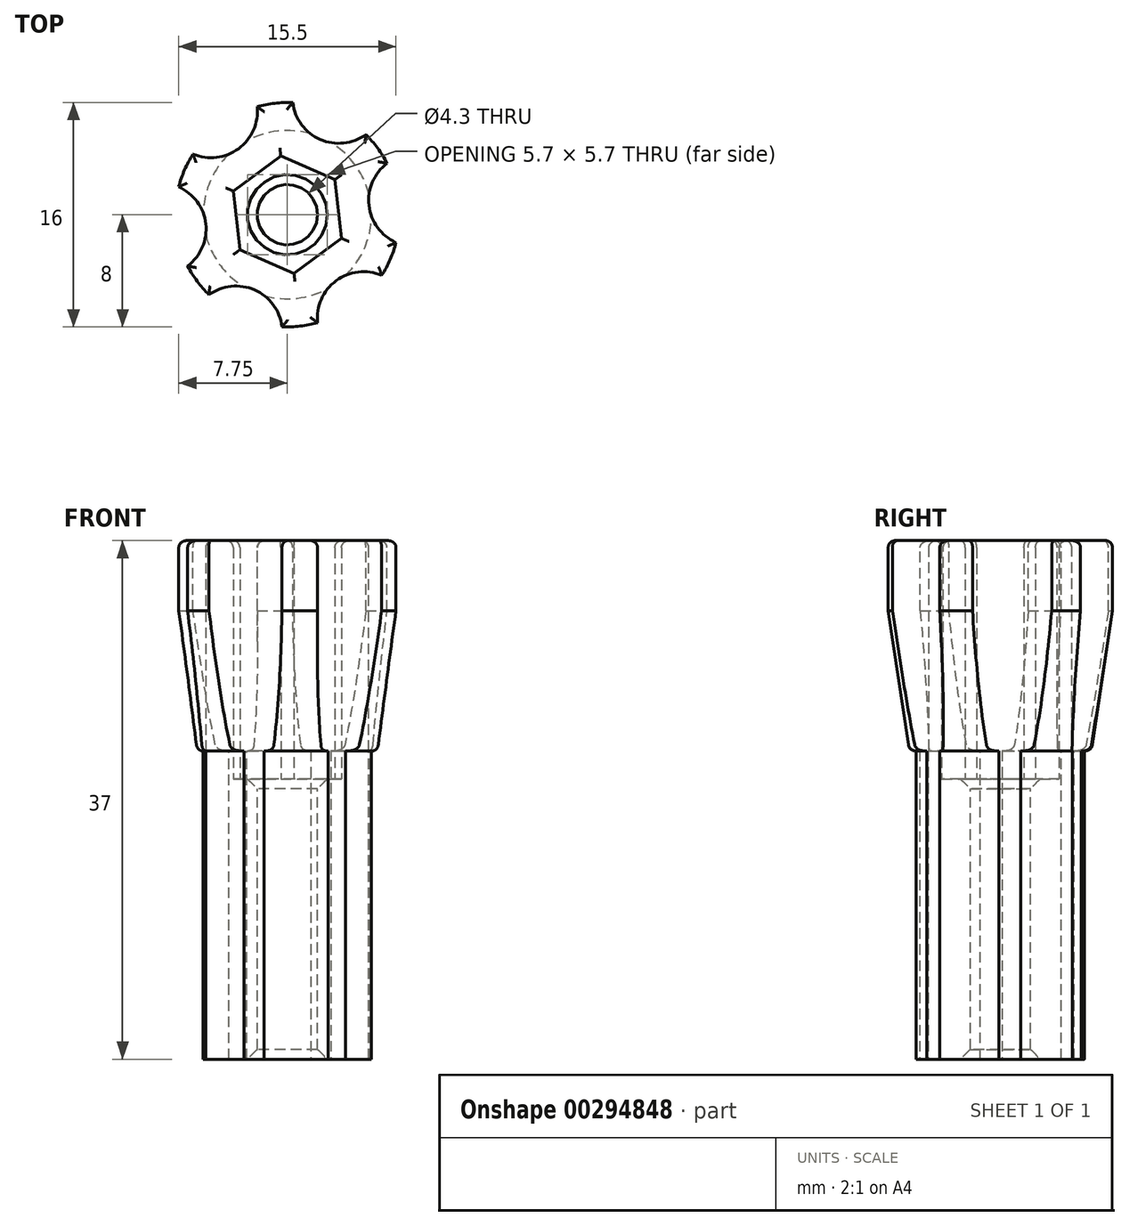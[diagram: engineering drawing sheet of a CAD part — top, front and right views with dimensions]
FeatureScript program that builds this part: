
annotation { "Feature Type Name" : "Feature", "Feature Type Description" : "" }
export const myFeature = defineFeature(function(context is Context, id is Id, definition is map)
    precondition{}
    {
        {
            var Q0;
            Q0=qCreatedBy(makeId("Top.planeOp"),FACE);
            var sketch = newSketch(context, id + "F0", { "sketchPlane" : qUnion([Q0])});
            skCircle(sketch, "E0", {"center": v(0, 0) * mm, "radius": 2.15 * mm});
            skCircle(sketch, "E1", {"center": v(0, 0) * mm, "radius": 6 * mm});
            skSolve(sketch);
        }
        {
            var Q0;
            Q0=makeQuery(id+"F0.imprint","IMPRINT",FACE,{"disambiguationData":[TD([[makeQuery(id+"F0.imprint","IMPRINT",EDGE,{"derivedFrom":sQuery(id+"F0.wireOp",EDGE,"E0")}),-1.0]])]});
            extrude(context, id + "F1", {"entities" : qUnion([Q0]), "depth" : 10 * mm});
        }
        {
            var Q0;
            Q0=qCreatedBy(makeId("Front.planeOp"),FACE);
            var sketch = newSketch(context, id + "F2", { "sketchPlane" : qUnion([Q0])});
            skLineSegment(sketch, "E2", {"start": v(0, 10) * mm, "end": v(0, 20) * mm});
            skLineSegment(sketch, "E3", {"start": v(0, 20) * mm, "end": v(8, 20) * mm});
            skLineSegment(sketch, "E4", {"start": v(8, 20) * mm, "end": v(0, 10) * mm});
            skLineSegment(sketch, "E5", {"start": v(0, 10) * mm, "end": v(6.5, 10) * mm});
            skLineSegment(sketch, "E6", {"start": v(6.5, 10) * mm, "end": v(8, 20) * mm});
            skLineSegment(sketch, "E7", {"start": v(0, 20) * mm, "end": v(2.1, 20) * mm});
            skLineSegment(sketch, "E8", {"start": v(2.1, 20) * mm, "end": v(2.1, 10) * mm});
            skSolve(sketch);
        }
        {
            var Q0;
            {var subQ0=sQuery(id+"F2.wireOp",EDGE,"E3");Q0=makeQuery(id+"F2.imprint","IMPRINT",FACE,{"disambiguationData":[TD([[makeQuery(id+"F2.imprint","IMPRINT",EDGE,{"derivedFrom":subQ0}),-1.0]])]});}
            var Q1;
            {var subQ0=sQuery(id+"F2.wireOp",EDGE,"E6");Q1=makeQuery(id+"F2.imprint","IMPRINT",FACE,{"disambiguationData":[TD([[makeQuery(id+"F2.imprint","IMPRINT",EDGE,{"derivedFrom":subQ0}),1.0]])]});}
            var Q2;
            Q2=sQuery(id+"F2.wireOp",EDGE,"E2");
            revolve(context, id + "F3", {"operationType" : NewBodyOperationType.ADD, "entities" : qUnion([Q0, Q1]), "axis" : qUnion([Q2]), "revolveType" : RevolveType.FULL});
        }
        {
            var Q0;
            Q0=makeQuery(id+"F3.opRevolve","SWEPT_FACE",FACE,{"disambiguationData":[OSD([sQuery(id+"F2.wireOp",EDGE,"E3")])]});
            var sketch = newSketch(context, id + "F4", { "sketchPlane" : qUnion([Q0])});
            skCircle(sketch, "E9.cCircle", {"center": v(0, 0) * mm, "radius": 5.25 * mm, "construction": true});
            skLineSegment(sketch, "E9.0", {"start": v(5.56, -2.42) * mm, "end": v(0.68, -6.02) * mm});
            skLineSegment(sketch, "E9.1", {"start": v(0.68, -6.02) * mm, "end": v(-4.88, -3.6) * mm});
            skLineSegment(sketch, "E9.2", {"start": v(-4.88, -3.6) * mm, "end": v(-5.56, 2.42) * mm});
            skLineSegment(sketch, "E9.3", {"start": v(-5.56, 2.42) * mm, "end": v(-0.68, 6.02) * mm});
            skLineSegment(sketch, "E9.4", {"start": v(-0.68, 6.02) * mm, "end": v(4.88, 3.6) * mm});
            skLineSegment(sketch, "E9.5", {"start": v(4.88, 3.6) * mm, "end": v(5.56, -2.42) * mm});
            skPoint(sketch, "E9.0.midPoint", {"position": v(3.12, -4.22) * mm});
            skCircle(sketch, "E10.cCircle", {"center": v(0, 0) * mm, "radius": 3.65 * mm, "construction": true});
            skLineSegment(sketch, "E10.0", {"start": v(-3.86, 1.69) * mm, "end": v(-0.47, 4.19) * mm});
            skLineSegment(sketch, "E10.1", {"start": v(-0.47, 4.19) * mm, "end": v(3.4, 2.5) * mm});
            skLineSegment(sketch, "E10.2", {"start": v(3.4, 2.5) * mm, "end": v(3.86, -1.69) * mm});
            skLineSegment(sketch, "E10.3", {"start": v(3.86, -1.69) * mm, "end": v(0.47, -4.19) * mm});
            skLineSegment(sketch, "E10.4", {"start": v(0.47, -4.19) * mm, "end": v(-3.4, -2.5) * mm});
            skLineSegment(sketch, "E10.5", {"start": v(-3.4, -2.5) * mm, "end": v(-3.86, 1.69) * mm});
            skPoint(sketch, "E10.0.midPoint", {"position": v(-2.17, 2.94) * mm});
            skSolve(sketch);
        }
        {
            var Q0;
            Q0=makeQuery(id+"F4.imprint","IMPRINT",FACE,{"disambiguationData":[TD([[makeQuery(id+"F4.imprint","IMPRINT",EDGE,{"derivedFrom":sQuery(id+"F4.wireOp",EDGE,"E9.0")}),1.0]])]});
            var Q1;
            Q1=makeQuery(id+"F4.imprint","IMPRINT",FACE,{"disambiguationData":[TD([[makeQuery(id+"F4.imprint","IMPRINT",EDGE,{"derivedFrom":sQuery(id+"F4.wireOp",EDGE,"E9.0")}),-1.0]])]});
            extrude(context, id + "F5", {"entities" : qUnion([Q0, Q1]), "operationType" : NewBodyOperationType.ADD, "depth" : 15 * mm});
        }
        {
            var Q0;
            Q0=makeQuery(id+"F5.opExtrude","CAP_FACE",FACE,{"disambiguationData":[OSD([sQuery(id+"F2.wireOp",EDGE,"E3"),sQuery(id+"F2.wireOp",EDGE,"E4"),sQuery(id+"F2.wireOp",EDGE,"E6"),sQuery(id+"F4.wireOp",EDGE,"E9.0"),sQuery(id+"F4.wireOp",EDGE,"E9.1"),sQuery(id+"F4.wireOp",EDGE,"E9.2"),sQuery(id+"F4.wireOp",EDGE,"E9.3"),sQuery(id+"F4.wireOp",EDGE,"E9.4"),sQuery(id+"F4.wireOp",EDGE,"E9.5")])],"isStart":false});
            var sketch = newSketch(context, id + "F6", { "sketchPlane" : qUnion([Q0])});
            skArc(sketch, "E11", {"start": v(1.46, 3.35) * mm, "mid": v(-0.92, 8.15) * mm, "end": v(-2.17, 2.94) * mm});
            skArc(sketch, "E12", {"start": v(-2.17, 2.94) * mm, "mid": v(-7.52, 3.28) * mm, "end": v(-3.63, -0.4) * mm});
            skArc(sketch, "E13", {"start": v(-6.73, 4.33) * mm, "mid": v(-3.48, 4.71) * mm, "end": v(-2.16, 7.7) * mm});
            skArc(sketch, "E14", {"start": v(-1.46, -3.35) * mm, "mid": v(0.92, -8.15) * mm, "end": v(2.17, -2.94) * mm});
            skArc(sketch, "E15", {"start": v(-3.63, -0.4) * mm, "mid": v(-6.6, -4.87) * mm, "end": v(-1.46, -3.35) * mm});
            skArc(sketch, "E16", {"start": v(2.17, -2.94) * mm, "mid": v(7.52, -3.28) * mm, "end": v(3.63, 0.4) * mm});
            skArc(sketch, "E17", {"start": v(3.63, 0.4) * mm, "mid": v(6.6, 4.87) * mm, "end": v(1.46, 3.35) * mm});
            skArc(sketch, "E18", {"start": v(0.39, 8) * mm, "mid": v(2.34, 5.37) * mm, "end": v(5.6, 5.72) * mm});
            skArc(sketch, "E19", {"start": v(7.11, 3.66) * mm, "mid": v(5.82, 0.66) * mm, "end": v(7.75, -1.99) * mm});
            skArc(sketch, "E20", {"start": v(6.73, -4.33) * mm, "mid": v(3.48, -4.71) * mm, "end": v(2.16, -7.7) * mm});
            skArc(sketch, "E21", {"start": v(-0.39, -8) * mm, "mid": v(-2.34, -5.37) * mm, "end": v(-5.6, -5.72) * mm});
            skArc(sketch, "E22", {"start": v(-7.11, -3.66) * mm, "mid": v(-5.82, -0.66) * mm, "end": v(-7.75, 1.99) * mm});
            skSolve(sketch);
        }
        {
            var Q0;
            {var subQ0=sQuery(id+"F6.wireOp",EDGE,"E13");var subQ1=sQuery(id+"F6.wireOp",EDGE,"E11");var subQ4=makeQuery(id+"F6.imprint","INTERSECT",VERTEX,{"derivedFrom":[subQ1,subQ0]});Q0=makeQuery(id+"F6.imprint","IMPRINT",FACE,{"disambiguationData":[TD([[makeQuery(id+"F6.imprint","IMPRINT",EDGE,{"disambiguationData":[TD([[subQ4,1.0]])],"derivedFrom":subQ0}),1.0]])]});}
            var Q1;
            {var subQ0=sQuery(id+"F6.wireOp",EDGE,"E13");var subQ1=sQuery(id+"F6.wireOp",EDGE,"E12");var subQ3=makeQuery(id+"F6.imprint","INTERSECT",VERTEX,{"derivedFrom":[subQ1,subQ0]});Q1=makeQuery(id+"F6.imprint","IMPRINT",FACE,{"disambiguationData":[TD([[makeQuery(id+"F6.imprint","IMPRINT",EDGE,{"disambiguationData":[TD([[subQ3,-1.0]])],"derivedFrom":subQ1}),1.0]])]});}
            var Q2;
            {var subQ0=sQuery(id+"F6.wireOp",EDGE,"E13");var subQ1=sQuery(id+"F6.wireOp",EDGE,"E11");var subQ3=makeQuery(id+"F6.imprint","INTERSECT",VERTEX,{"derivedFrom":[subQ1,subQ0]});Q2=makeQuery(id+"F6.imprint","IMPRINT",FACE,{"disambiguationData":[TD([[makeQuery(id+"F6.imprint","IMPRINT",EDGE,{"disambiguationData":[TD([[subQ3,1.0]])],"derivedFrom":subQ1}),1.0]])]});}
            var Q3;
            {var subQ0=sQuery(id+"F6.wireOp",EDGE,"E22");var subQ1=sQuery(id+"F6.wireOp",EDGE,"E12");var subQ4=makeQuery(id+"F6.imprint","INTERSECT",VERTEX,{"derivedFrom":[subQ1,subQ0]});Q3=makeQuery(id+"F6.imprint","IMPRINT",FACE,{"disambiguationData":[TD([[makeQuery(id+"F6.imprint","IMPRINT",EDGE,{"disambiguationData":[TD([[subQ4,1.0]])],"derivedFrom":subQ0}),1.0]])]});}
            var Q4;
            {var subQ0=sQuery(id+"F6.wireOp",EDGE,"E22");var subQ1=sQuery(id+"F6.wireOp",EDGE,"E12");var subQ3=makeQuery(id+"F6.imprint","INTERSECT",VERTEX,{"derivedFrom":[subQ1,subQ0]});Q4=makeQuery(id+"F6.imprint","IMPRINT",FACE,{"disambiguationData":[TD([[makeQuery(id+"F6.imprint","IMPRINT",EDGE,{"disambiguationData":[TD([[subQ3,1.0]])],"derivedFrom":subQ1}),1.0]])]});}
            var Q5;
            {var subQ0=sQuery(id+"F6.wireOp",EDGE,"E22");var subQ1=sQuery(id+"F6.wireOp",EDGE,"E15");var subQ3=makeQuery(id+"F6.imprint","INTERSECT",VERTEX,{"derivedFrom":[subQ1,subQ0]});Q5=makeQuery(id+"F6.imprint","IMPRINT",FACE,{"disambiguationData":[TD([[makeQuery(id+"F6.imprint","IMPRINT",EDGE,{"disambiguationData":[TD([[subQ3,-1.0]])],"derivedFrom":subQ1}),1.0]])]});}
            var Q6;
            {var subQ0=sQuery(id+"F6.wireOp",EDGE,"E21");var subQ1=sQuery(id+"F6.wireOp",EDGE,"E14");var subQ4=makeQuery(id+"F6.imprint","INTERSECT",VERTEX,{"derivedFrom":[subQ1,subQ0]});Q6=makeQuery(id+"F6.imprint","IMPRINT",FACE,{"disambiguationData":[TD([[makeQuery(id+"F6.imprint","IMPRINT",EDGE,{"disambiguationData":[TD([[subQ4,-1.0]])],"derivedFrom":subQ0}),1.0]])]});}
            var Q7;
            {var subQ0=sQuery(id+"F6.wireOp",EDGE,"E21");var subQ1=sQuery(id+"F6.wireOp",EDGE,"E15");var subQ3=makeQuery(id+"F6.imprint","INTERSECT",VERTEX,{"derivedFrom":[subQ1,subQ0]});Q7=makeQuery(id+"F6.imprint","IMPRINT",FACE,{"disambiguationData":[TD([[makeQuery(id+"F6.imprint","IMPRINT",EDGE,{"disambiguationData":[TD([[subQ3,1.0]])],"derivedFrom":subQ1}),1.0]])]});}
            var Q8;
            {var subQ0=sQuery(id+"F6.wireOp",EDGE,"E21");var subQ1=sQuery(id+"F6.wireOp",EDGE,"E14");var subQ3=makeQuery(id+"F6.imprint","INTERSECT",VERTEX,{"derivedFrom":[subQ1,subQ0]});Q8=makeQuery(id+"F6.imprint","IMPRINT",FACE,{"disambiguationData":[TD([[makeQuery(id+"F6.imprint","IMPRINT",EDGE,{"disambiguationData":[TD([[subQ3,-1.0]])],"derivedFrom":subQ1}),1.0]])]});}
            var Q9;
            {var subQ0=sQuery(id+"F6.wireOp",EDGE,"E20");var subQ1=sQuery(id+"F6.wireOp",EDGE,"E14");var subQ4=makeQuery(id+"F6.imprint","INTERSECT",VERTEX,{"derivedFrom":[subQ1,subQ0]});Q9=makeQuery(id+"F6.imprint","IMPRINT",FACE,{"disambiguationData":[TD([[makeQuery(id+"F6.imprint","IMPRINT",EDGE,{"disambiguationData":[TD([[subQ4,1.0]])],"derivedFrom":subQ0}),1.0]])]});}
            var Q10;
            {var subQ0=sQuery(id+"F6.wireOp",EDGE,"E20");var subQ1=sQuery(id+"F6.wireOp",EDGE,"E16");var subQ3=makeQuery(id+"F6.imprint","INTERSECT",VERTEX,{"derivedFrom":[subQ1,subQ0]});Q10=makeQuery(id+"F6.imprint","IMPRINT",FACE,{"disambiguationData":[TD([[makeQuery(id+"F6.imprint","IMPRINT",EDGE,{"disambiguationData":[TD([[subQ3,-1.0]])],"derivedFrom":subQ1}),1.0]])]});}
            var Q11;
            {var subQ0=sQuery(id+"F6.wireOp",EDGE,"E20");var subQ1=sQuery(id+"F6.wireOp",EDGE,"E14");var subQ3=makeQuery(id+"F6.imprint","INTERSECT",VERTEX,{"derivedFrom":[subQ1,subQ0]});Q11=makeQuery(id+"F6.imprint","IMPRINT",FACE,{"disambiguationData":[TD([[makeQuery(id+"F6.imprint","IMPRINT",EDGE,{"disambiguationData":[TD([[subQ3,1.0]])],"derivedFrom":subQ1}),1.0]])]});}
            var Q12;
            {var subQ0=sQuery(id+"F6.wireOp",EDGE,"E19");var subQ1=sQuery(id+"F6.wireOp",EDGE,"E16");var subQ4=makeQuery(id+"F6.imprint","INTERSECT",VERTEX,{"derivedFrom":[subQ1,subQ0]});Q12=makeQuery(id+"F6.imprint","IMPRINT",FACE,{"disambiguationData":[TD([[makeQuery(id+"F6.imprint","IMPRINT",EDGE,{"disambiguationData":[TD([[subQ4,1.0]])],"derivedFrom":subQ0}),1.0]])]});}
            var Q13;
            {var subQ0=sQuery(id+"F6.wireOp",EDGE,"E19");var subQ1=sQuery(id+"F6.wireOp",EDGE,"E16");var subQ3=makeQuery(id+"F6.imprint","INTERSECT",VERTEX,{"derivedFrom":[subQ1,subQ0]});Q13=makeQuery(id+"F6.imprint","IMPRINT",FACE,{"disambiguationData":[TD([[makeQuery(id+"F6.imprint","IMPRINT",EDGE,{"disambiguationData":[TD([[subQ3,1.0]])],"derivedFrom":subQ1}),1.0]])]});}
            var Q14;
            {var subQ0=sQuery(id+"F6.wireOp",EDGE,"E19");var subQ1=sQuery(id+"F6.wireOp",EDGE,"E17");var subQ3=makeQuery(id+"F6.imprint","INTERSECT",VERTEX,{"derivedFrom":[subQ1,subQ0]});Q14=makeQuery(id+"F6.imprint","IMPRINT",FACE,{"disambiguationData":[TD([[makeQuery(id+"F6.imprint","IMPRINT",EDGE,{"disambiguationData":[TD([[subQ3,-1.0]])],"derivedFrom":subQ1}),1.0]])]});}
            var Q15;
            {var subQ0=sQuery(id+"F6.wireOp",EDGE,"E18");var subQ1=sQuery(id+"F6.wireOp",EDGE,"E11");var subQ4=makeQuery(id+"F6.imprint","INTERSECT",VERTEX,{"derivedFrom":[subQ1,subQ0]});Q15=makeQuery(id+"F6.imprint","IMPRINT",FACE,{"disambiguationData":[TD([[makeQuery(id+"F6.imprint","IMPRINT",EDGE,{"disambiguationData":[TD([[subQ4,-1.0]])],"derivedFrom":subQ0}),1.0]])]});}
            var Q16;
            {var subQ0=sQuery(id+"F6.wireOp",EDGE,"E18");var subQ1=sQuery(id+"F6.wireOp",EDGE,"E11");var subQ3=makeQuery(id+"F6.imprint","INTERSECT",VERTEX,{"derivedFrom":[subQ1,subQ0]});Q16=makeQuery(id+"F6.imprint","IMPRINT",FACE,{"disambiguationData":[TD([[makeQuery(id+"F6.imprint","IMPRINT",EDGE,{"disambiguationData":[TD([[subQ3,-1.0]])],"derivedFrom":subQ1}),1.0]])]});}
            var Q17;
            {var subQ0=sQuery(id+"F6.wireOp",EDGE,"E18");var subQ1=sQuery(id+"F6.wireOp",EDGE,"E17");var subQ3=makeQuery(id+"F6.imprint","INTERSECT",VERTEX,{"derivedFrom":[subQ1,subQ0]});Q17=makeQuery(id+"F6.imprint","IMPRINT",FACE,{"disambiguationData":[TD([[makeQuery(id+"F6.imprint","IMPRINT",EDGE,{"disambiguationData":[TD([[subQ3,1.0]])],"derivedFrom":subQ1}),1.0]])]});}
            extrude(context, id + "F7", {"entities" : qUnion([Q0, Q1, Q2, Q3, Q4, Q5, Q6, Q7, Q8, Q9, Q10, Q11, Q12, Q13, Q14, Q15, Q16, Q17]), "operationType" : NewBodyOperationType.REMOVE, "oppositeDirection" : true, "depth" : 25 * mm});
        }
        {
            var Q0;
            Q0=makeQuery(id+"F5.opExtrude","CAP_FACE",FACE,{"disambiguationData":[OSD([sQuery(id+"F2.wireOp",EDGE,"E3"),sQuery(id+"F2.wireOp",EDGE,"E4"),sQuery(id+"F2.wireOp",EDGE,"E6"),sQuery(id+"F4.wireOp",EDGE,"E9.0"),sQuery(id+"F4.wireOp",EDGE,"E9.1"),sQuery(id+"F4.wireOp",EDGE,"E9.2"),sQuery(id+"F4.wireOp",EDGE,"E9.3"),sQuery(id+"F4.wireOp",EDGE,"E9.4"),sQuery(id+"F4.wireOp",EDGE,"E9.5")])],"isStart":false});
            extrude(context, id + "F8", {"entities" : qUnion([Q0]), "operationType" : NewBodyOperationType.REMOVE, "oppositeDirection" : true, "depth" : 5 * mm});
        }
        {
            var Q0;
            Q0=makeQuery(id+"F1.opExtrude","CAP_FACE",FACE,{"disambiguationData":[OSD([sQuery(id+"F0.wireOp",EDGE,"E0"),sQuery(id+"F0.wireOp",EDGE,"E1")])],"isStart":true});
            extrude(context, id + "F9", {"entities" : qUnion([Q0]), "operationType" : NewBodyOperationType.REMOVE, "oppositeDirection" : true, "depth" : 10 * mm});
        }
        {
            var Q0;
            Q0=makeQuery(id+"F8.boolean.opBoolean","COPY",FACE,{"derivedFrom":makeQuery(id+"F8.opExtrude","CAP_FACE",FACE,{"disambiguationData":[OSD([sQuery(id+"F2.wireOp",EDGE,"E3"),sQuery(id+"F2.wireOp",EDGE,"E4"),sQuery(id+"F2.wireOp",EDGE,"E6"),sQuery(id+"F4.wireOp",EDGE,"E10.0"),sQuery(id+"F4.wireOp",EDGE,"E10.1"),sQuery(id+"F4.wireOp",EDGE,"E10.2"),sQuery(id+"F4.wireOp",EDGE,"E10.3"),sQuery(id+"F4.wireOp",EDGE,"E10.4"),sQuery(id+"F4.wireOp",EDGE,"E10.5")])],"isStart":false})});
            extrude(context, id + "F10", {"entities" : qUnion([Q0]), "operationType" : NewBodyOperationType.REMOVE, "oppositeDirection" : true, "depth" : 5 * mm});
        }
        {
            var Q0;
            {var subQ0=sQuery(id+"F2.wireOp",EDGE,"E6");var subQ1=sQuery(id+"F2.wireOp",EDGE,"E4");var subQ2=sQuery(id+"F2.wireOp",EDGE,"E3");var subQ3=sQuery(id+"F6.wireOp",EDGE,"E21");var subQ5=makeQuery(id+"F5.opExtrude","CAP_EDGE",EDGE,{"disambiguationData":[OSD([subQ2,subQ1,subQ0])],"isStart":false});Q0=makeQuery(id+"F10.boolean.opBoolean","COPY",EDGE,{"derivedFrom":makeQuery(id+"F10.opExtrude","CAP_EDGE",EDGE,{"disambiguationData":[OSD([subQ2,subQ1,subQ0]),TDD([makeQuery(id+"F8.boolean.opBoolean","COPY",EDGE,{"derivedFrom":makeQuery(id+"F8.opExtrude","CAP_EDGE",EDGE,{"disambiguationData":[OSD([subQ2,subQ1,subQ0]),TDD([makeQuery(id+"F7.boolean.opBoolean","SPLIT",EDGE,{"disambiguationData":[TD([makeQuery(id+"F7.opExtrude","SWEPT_FACE",FACE,{"disambiguationData":[OSD([subQ3]),TDD([makeQuery(id+"F6.imprint","IMPRINT",EDGE,{"disambiguationData":[TD([[makeQuery(id+"F6.imprint","INTERSECT",VERTEX,{"derivedFrom":[sQuery(id+"F6.wireOp",EDGE,"E14"),subQ3]}),-1.0]])],"derivedFrom":subQ3})])]})])],"derivedFrom":subQ5})])],"isStart":false})})])],"isStart":false})});}
            var Q1;
            {var subQ0=sQuery(id+"F2.wireOp",EDGE,"E6");var subQ1=sQuery(id+"F2.wireOp",EDGE,"E4");var subQ2=sQuery(id+"F2.wireOp",EDGE,"E3");var subQ3=sQuery(id+"F6.wireOp",EDGE,"E20");var subQ5=makeQuery(id+"F5.opExtrude","CAP_EDGE",EDGE,{"disambiguationData":[OSD([subQ2,subQ1,subQ0])],"isStart":false});Q1=makeQuery(id+"F10.boolean.opBoolean","COPY",EDGE,{"derivedFrom":makeQuery(id+"F10.opExtrude","CAP_EDGE",EDGE,{"disambiguationData":[OSD([subQ2,subQ1,subQ0]),TDD([makeQuery(id+"F8.boolean.opBoolean","COPY",EDGE,{"derivedFrom":makeQuery(id+"F8.opExtrude","CAP_EDGE",EDGE,{"disambiguationData":[OSD([subQ2,subQ1,subQ0]),TDD([makeQuery(id+"F7.boolean.opBoolean","SPLIT",EDGE,{"disambiguationData":[TD([makeQuery(id+"F7.opExtrude","SWEPT_FACE",FACE,{"disambiguationData":[OSD([subQ3]),TDD([makeQuery(id+"F6.imprint","IMPRINT",EDGE,{"disambiguationData":[TD([[makeQuery(id+"F6.imprint","INTERSECT",VERTEX,{"derivedFrom":[sQuery(id+"F6.wireOp",EDGE,"E16"),subQ3]}),-1.0]])],"derivedFrom":subQ3})])]})])],"derivedFrom":subQ5})])],"isStart":false})})])],"isStart":false})});}
            var Q2;
            {var subQ0=sQuery(id+"F2.wireOp",EDGE,"E6");var subQ1=sQuery(id+"F2.wireOp",EDGE,"E4");var subQ2=sQuery(id+"F2.wireOp",EDGE,"E3");var subQ3=sQuery(id+"F6.wireOp",EDGE,"E19");var subQ5=makeQuery(id+"F5.opExtrude","CAP_EDGE",EDGE,{"disambiguationData":[OSD([subQ2,subQ1,subQ0])],"isStart":false});Q2=makeQuery(id+"F10.boolean.opBoolean","COPY",EDGE,{"derivedFrom":makeQuery(id+"F10.opExtrude","CAP_EDGE",EDGE,{"disambiguationData":[OSD([subQ2,subQ1,subQ0]),TDD([makeQuery(id+"F8.boolean.opBoolean","COPY",EDGE,{"derivedFrom":makeQuery(id+"F8.opExtrude","CAP_EDGE",EDGE,{"disambiguationData":[OSD([subQ2,subQ1,subQ0]),TDD([makeQuery(id+"F7.boolean.opBoolean","SPLIT",EDGE,{"disambiguationData":[TD([makeQuery(id+"F7.opExtrude","SWEPT_FACE",FACE,{"disambiguationData":[OSD([subQ3]),TDD([makeQuery(id+"F6.imprint","IMPRINT",EDGE,{"disambiguationData":[TD([[makeQuery(id+"F6.imprint","INTERSECT",VERTEX,{"derivedFrom":[sQuery(id+"F6.wireOp",EDGE,"E17"),subQ3]}),-1.0]])],"derivedFrom":subQ3})])]})])],"derivedFrom":subQ5})])],"isStart":false})})])],"isStart":false})});}
            var Q3;
            {var subQ0=sQuery(id+"F2.wireOp",EDGE,"E6");var subQ1=sQuery(id+"F2.wireOp",EDGE,"E4");var subQ2=sQuery(id+"F2.wireOp",EDGE,"E3");var subQ5=makeQuery(id+"F5.opExtrude","CAP_EDGE",EDGE,{"disambiguationData":[OSD([subQ2,subQ1,subQ0])],"isStart":false});var subQ6=sQuery(id+"F6.wireOp",EDGE,"E18");Q3=makeQuery(id+"F10.boolean.opBoolean","COPY",EDGE,{"derivedFrom":makeQuery(id+"F10.opExtrude","CAP_EDGE",EDGE,{"disambiguationData":[OSD([subQ2,subQ1,subQ0]),TDD([makeQuery(id+"F8.boolean.opBoolean","COPY",EDGE,{"derivedFrom":makeQuery(id+"F8.opExtrude","CAP_EDGE",EDGE,{"disambiguationData":[OSD([subQ2,subQ1,subQ0]),TDD([makeQuery(id+"F7.boolean.opBoolean","SPLIT",EDGE,{"disambiguationData":[TD([makeQuery(id+"F7.opExtrude","SWEPT_FACE",FACE,{"disambiguationData":[OSD([subQ6]),TDD([makeQuery(id+"F6.imprint","IMPRINT",EDGE,{"disambiguationData":[TD([[makeQuery(id+"F6.imprint","INTERSECT",VERTEX,{"derivedFrom":[sQuery(id+"F6.wireOp",EDGE,"E11"),subQ6]}),-1.0]])],"derivedFrom":subQ6})])]})])],"derivedFrom":subQ5})])],"isStart":false})})])],"isStart":false})});}
            var Q4;
            {var subQ0=sQuery(id+"F2.wireOp",EDGE,"E6");var subQ1=sQuery(id+"F2.wireOp",EDGE,"E4");var subQ2=sQuery(id+"F2.wireOp",EDGE,"E3");var subQ3=sQuery(id+"F6.wireOp",EDGE,"E13");var subQ5=makeQuery(id+"F5.opExtrude","CAP_EDGE",EDGE,{"disambiguationData":[OSD([subQ2,subQ1,subQ0])],"isStart":false});Q4=makeQuery(id+"F10.boolean.opBoolean","COPY",EDGE,{"derivedFrom":makeQuery(id+"F10.opExtrude","CAP_EDGE",EDGE,{"disambiguationData":[OSD([subQ2,subQ1,subQ0]),TDD([makeQuery(id+"F8.boolean.opBoolean","COPY",EDGE,{"derivedFrom":makeQuery(id+"F8.opExtrude","CAP_EDGE",EDGE,{"disambiguationData":[OSD([subQ2,subQ1,subQ0]),TDD([makeQuery(id+"F7.boolean.opBoolean","SPLIT",EDGE,{"disambiguationData":[TD([makeQuery(id+"F7.opExtrude","SWEPT_FACE",FACE,{"disambiguationData":[OSD([subQ3]),TDD([makeQuery(id+"F6.imprint","IMPRINT",EDGE,{"disambiguationData":[TD([[makeQuery(id+"F6.imprint","INTERSECT",VERTEX,{"derivedFrom":[sQuery(id+"F6.wireOp",EDGE,"E12"),subQ3]}),-1.0]])],"derivedFrom":subQ3})])]})])],"derivedFrom":subQ5})])],"isStart":false})})])],"isStart":false})});}
            var Q5;
            {var subQ0=sQuery(id+"F2.wireOp",EDGE,"E6");var subQ1=sQuery(id+"F2.wireOp",EDGE,"E4");var subQ2=sQuery(id+"F2.wireOp",EDGE,"E3");var subQ3=sQuery(id+"F6.wireOp",EDGE,"E13");var subQ5=makeQuery(id+"F5.opExtrude","CAP_EDGE",EDGE,{"disambiguationData":[OSD([subQ2,subQ1,subQ0])],"isStart":false});Q5=makeQuery(id+"F10.boolean.opBoolean","COPY",EDGE,{"derivedFrom":makeQuery(id+"F10.opExtrude","CAP_EDGE",EDGE,{"disambiguationData":[OSD([subQ2,subQ1,subQ0]),TDD([makeQuery(id+"F8.boolean.opBoolean","COPY",EDGE,{"derivedFrom":makeQuery(id+"F8.opExtrude","CAP_EDGE",EDGE,{"disambiguationData":[OSD([subQ2,subQ1,subQ0]),TDD([makeQuery(id+"F7.boolean.opBoolean","SPLIT",EDGE,{"disambiguationData":[TD([makeQuery(id+"F7.opExtrude","SWEPT_FACE",FACE,{"disambiguationData":[OSD([subQ3]),TDD([makeQuery(id+"F6.imprint","IMPRINT",EDGE,{"disambiguationData":[TD([[makeQuery(id+"F6.imprint","INTERSECT",VERTEX,{"derivedFrom":[sQuery(id+"F6.wireOp",EDGE,"E11"),subQ3]}),1.0]])],"derivedFrom":subQ3})])]})])],"derivedFrom":subQ5})])],"isStart":false})})])],"isStart":false})});}
            var Q6;
            Q6=makeQuery(id+"F10.boolean.opBoolean","COPY",EDGE,{"derivedFrom":makeQuery(id+"F10.opExtrude","CAP_EDGE",EDGE,{"disambiguationData":[OSD([sQuery(id+"F6.wireOp",EDGE,"E21")])],"isStart":false})});
            var Q7;
            Q7=makeQuery(id+"F10.boolean.opBoolean","COPY",FACE,{"derivedFrom":makeQuery(id+"F10.opExtrude","CAP_FACE",FACE,{"disambiguationData":[OSD([sQuery(id+"F2.wireOp",EDGE,"E3"),sQuery(id+"F2.wireOp",EDGE,"E4"),sQuery(id+"F2.wireOp",EDGE,"E6"),sQuery(id+"F4.wireOp",EDGE,"E10.0"),sQuery(id+"F4.wireOp",EDGE,"E10.1"),sQuery(id+"F4.wireOp",EDGE,"E10.2"),sQuery(id+"F4.wireOp",EDGE,"E10.3"),sQuery(id+"F4.wireOp",EDGE,"E10.4"),sQuery(id+"F4.wireOp",EDGE,"E10.5")])],"isStart":false})});
            fillet(context, id + "F11", {"entities" : qUnion([Q0, Q1, Q2, Q3, Q4, Q5, Q6, Q7]), "radius" : 0.5 * mm, "tangentPropagation" : true, "allowEdgeOverflow" : false});
        }
        {
            var Q0;
            {var subQ0=sQuery(id+"F2.wireOp",EDGE,"E5");var subQ1=sQuery(id+"F2.wireOp",EDGE,"E6");Q0=makeQuery(id+"F7.boolean.opBoolean","SPLIT",EDGE,{"disambiguationData":[TD([makeQuery(id+"F3.opRevolve","SWEPT_FACE",FACE,{"disambiguationData":[OSD([subQ0])]}),makeQuery(id+"F3.opRevolve","SWEPT_FACE",FACE,{"disambiguationData":[OSD([subQ1])]}),makeQuery(id+"F7.opExtrude","SWEPT_FACE",FACE,{"disambiguationData":[OSD([sQuery(id+"F6.wireOp",EDGE,"E13")])]}),makeQuery(id+"F7.opExtrude","SWEPT_FACE",FACE,{"disambiguationData":[OSD([sQuery(id+"F6.wireOp",EDGE,"E18")])]})])],"derivedFrom":makeQuery(id+"F3.opRevolve","SWEPT_EDGE",EDGE,{"disambiguationData":[OSD([subQ0,subQ1])]})});}
            var Q1;
            {var subQ0=sQuery(id+"F2.wireOp",EDGE,"E5");var subQ1=sQuery(id+"F2.wireOp",EDGE,"E6");Q1=makeQuery(id+"F7.boolean.opBoolean","SPLIT",EDGE,{"disambiguationData":[TD([makeQuery(id+"F3.opRevolve","SWEPT_FACE",FACE,{"disambiguationData":[OSD([subQ0])]}),makeQuery(id+"F3.opRevolve","SWEPT_FACE",FACE,{"disambiguationData":[OSD([subQ1])]}),makeQuery(id+"F7.opExtrude","SWEPT_FACE",FACE,{"disambiguationData":[OSD([sQuery(id+"F6.wireOp",EDGE,"E18")])]}),makeQuery(id+"F7.opExtrude","SWEPT_FACE",FACE,{"disambiguationData":[OSD([sQuery(id+"F6.wireOp",EDGE,"E19")])]})])],"derivedFrom":makeQuery(id+"F3.opRevolve","SWEPT_EDGE",EDGE,{"disambiguationData":[OSD([subQ0,subQ1])]})});}
            var Q2;
            {var subQ0=sQuery(id+"F2.wireOp",EDGE,"E5");var subQ1=sQuery(id+"F2.wireOp",EDGE,"E6");Q2=makeQuery(id+"F7.boolean.opBoolean","SPLIT",EDGE,{"disambiguationData":[TD([makeQuery(id+"F3.opRevolve","SWEPT_FACE",FACE,{"disambiguationData":[OSD([subQ0])]}),makeQuery(id+"F3.opRevolve","SWEPT_FACE",FACE,{"disambiguationData":[OSD([subQ1])]}),makeQuery(id+"F7.opExtrude","SWEPT_FACE",FACE,{"disambiguationData":[OSD([sQuery(id+"F6.wireOp",EDGE,"E13")])]}),makeQuery(id+"F7.opExtrude","SWEPT_FACE",FACE,{"disambiguationData":[OSD([sQuery(id+"F6.wireOp",EDGE,"E22")])]})])],"derivedFrom":makeQuery(id+"F3.opRevolve","SWEPT_EDGE",EDGE,{"disambiguationData":[OSD([subQ0,subQ1])]})});}
            var Q3;
            {var subQ0=sQuery(id+"F2.wireOp",EDGE,"E5");var subQ1=sQuery(id+"F2.wireOp",EDGE,"E6");Q3=makeQuery(id+"F7.boolean.opBoolean","SPLIT",EDGE,{"disambiguationData":[TD([makeQuery(id+"F3.opRevolve","SWEPT_FACE",FACE,{"disambiguationData":[OSD([subQ0])]}),makeQuery(id+"F3.opRevolve","SWEPT_FACE",FACE,{"disambiguationData":[OSD([subQ1])]}),makeQuery(id+"F7.opExtrude","SWEPT_FACE",FACE,{"disambiguationData":[OSD([sQuery(id+"F6.wireOp",EDGE,"E21")])]}),makeQuery(id+"F7.opExtrude","SWEPT_FACE",FACE,{"disambiguationData":[OSD([sQuery(id+"F6.wireOp",EDGE,"E22")])]})])],"derivedFrom":makeQuery(id+"F3.opRevolve","SWEPT_EDGE",EDGE,{"disambiguationData":[OSD([subQ0,subQ1])]})});}
            var Q4;
            {var subQ0=sQuery(id+"F2.wireOp",EDGE,"E5");var subQ1=sQuery(id+"F2.wireOp",EDGE,"E6");Q4=makeQuery(id+"F7.boolean.opBoolean","SPLIT",EDGE,{"disambiguationData":[TD([makeQuery(id+"F3.opRevolve","SWEPT_FACE",FACE,{"disambiguationData":[OSD([subQ0])]}),makeQuery(id+"F3.opRevolve","SWEPT_FACE",FACE,{"disambiguationData":[OSD([subQ1])]}),makeQuery(id+"F7.opExtrude","SWEPT_FACE",FACE,{"disambiguationData":[OSD([sQuery(id+"F6.wireOp",EDGE,"E20")])]}),makeQuery(id+"F7.opExtrude","SWEPT_FACE",FACE,{"disambiguationData":[OSD([sQuery(id+"F6.wireOp",EDGE,"E21")])]})])],"derivedFrom":makeQuery(id+"F3.opRevolve","SWEPT_EDGE",EDGE,{"disambiguationData":[OSD([subQ0,subQ1])]})});}
            var Q5;
            {var subQ0=sQuery(id+"F2.wireOp",EDGE,"E5");var subQ1=sQuery(id+"F2.wireOp",EDGE,"E6");Q5=makeQuery(id+"F7.boolean.opBoolean","SPLIT",EDGE,{"disambiguationData":[TD([makeQuery(id+"F3.opRevolve","SWEPT_FACE",FACE,{"disambiguationData":[OSD([subQ0])]}),makeQuery(id+"F3.opRevolve","SWEPT_FACE",FACE,{"disambiguationData":[OSD([subQ1])]}),makeQuery(id+"F7.opExtrude","SWEPT_FACE",FACE,{"disambiguationData":[OSD([sQuery(id+"F6.wireOp",EDGE,"E19")])]}),makeQuery(id+"F7.opExtrude","SWEPT_FACE",FACE,{"disambiguationData":[OSD([sQuery(id+"F6.wireOp",EDGE,"E20")])]})])],"derivedFrom":makeQuery(id+"F3.opRevolve","SWEPT_EDGE",EDGE,{"disambiguationData":[OSD([subQ0,subQ1])]})});}
            var Q6;
            {var subQ0=sQuery(id+"F6.wireOp",EDGE,"E22");Q6=makeQuery(id+"F7.boolean.opBoolean","COPY",EDGE,{"disambiguationData":[topologyDisambiguationEdgeConnected([makeQuery(id+"F7.opExtrude","SWEPT_FACE",FACE,{"disambiguationData":[OSD([subQ0])]}),makeQuery(id+"F7.opExtrude","CAP_FACE",FACE,{"disambiguationData":[OSD([sQuery(id+"F2.wireOp",EDGE,"E3"),sQuery(id+"F2.wireOp",EDGE,"E4"),sQuery(id+"F2.wireOp",EDGE,"E6"),subQ0])],"isStart":false})])],"derivedFrom":makeQuery(id+"F7.opExtrude","CAP_EDGE",EDGE,{"disambiguationData":[OSD([subQ0])],"isStart":false})});}
            var Q7;
            {var subQ0=sQuery(id+"F6.wireOp",EDGE,"E21");Q7=makeQuery(id+"F7.boolean.opBoolean","COPY",EDGE,{"disambiguationData":[topologyDisambiguationEdgeConnected([makeQuery(id+"F7.opExtrude","SWEPT_FACE",FACE,{"disambiguationData":[OSD([subQ0])]}),makeQuery(id+"F7.opExtrude","CAP_FACE",FACE,{"disambiguationData":[OSD([sQuery(id+"F2.wireOp",EDGE,"E3"),sQuery(id+"F2.wireOp",EDGE,"E4"),sQuery(id+"F2.wireOp",EDGE,"E6"),subQ0])],"isStart":false})])],"derivedFrom":makeQuery(id+"F7.opExtrude","CAP_EDGE",EDGE,{"disambiguationData":[OSD([subQ0])],"isStart":false})});}
            var Q8;
            {var subQ0=sQuery(id+"F6.wireOp",EDGE,"E20");Q8=makeQuery(id+"F7.boolean.opBoolean","COPY",EDGE,{"disambiguationData":[topologyDisambiguationEdgeConnected([makeQuery(id+"F7.opExtrude","SWEPT_FACE",FACE,{"disambiguationData":[OSD([subQ0])]}),makeQuery(id+"F7.opExtrude","CAP_FACE",FACE,{"disambiguationData":[OSD([sQuery(id+"F2.wireOp",EDGE,"E3"),sQuery(id+"F2.wireOp",EDGE,"E4"),sQuery(id+"F2.wireOp",EDGE,"E6"),subQ0])],"isStart":false})])],"derivedFrom":makeQuery(id+"F7.opExtrude","CAP_EDGE",EDGE,{"disambiguationData":[OSD([subQ0])],"isStart":false})});}
            var Q9;
            {var subQ0=sQuery(id+"F6.wireOp",EDGE,"E19");Q9=makeQuery(id+"F7.boolean.opBoolean","COPY",EDGE,{"disambiguationData":[topologyDisambiguationEdgeConnected([makeQuery(id+"F7.opExtrude","SWEPT_FACE",FACE,{"disambiguationData":[OSD([subQ0])]}),makeQuery(id+"F7.opExtrude","CAP_FACE",FACE,{"disambiguationData":[OSD([sQuery(id+"F2.wireOp",EDGE,"E3"),sQuery(id+"F2.wireOp",EDGE,"E4"),sQuery(id+"F2.wireOp",EDGE,"E6"),subQ0])],"isStart":false})])],"derivedFrom":makeQuery(id+"F7.opExtrude","CAP_EDGE",EDGE,{"disambiguationData":[OSD([subQ0])],"isStart":false})});}
            var Q10;
            {var subQ0=sQuery(id+"F6.wireOp",EDGE,"E18");Q10=makeQuery(id+"F7.boolean.opBoolean","COPY",EDGE,{"disambiguationData":[topologyDisambiguationEdgeConnected([makeQuery(id+"F7.opExtrude","SWEPT_FACE",FACE,{"disambiguationData":[OSD([subQ0])]}),makeQuery(id+"F7.opExtrude","CAP_FACE",FACE,{"disambiguationData":[OSD([sQuery(id+"F2.wireOp",EDGE,"E3"),sQuery(id+"F2.wireOp",EDGE,"E4"),sQuery(id+"F2.wireOp",EDGE,"E6"),subQ0])],"isStart":false})])],"derivedFrom":makeQuery(id+"F7.opExtrude","CAP_EDGE",EDGE,{"disambiguationData":[OSD([subQ0])],"isStart":false})});}
            var Q11;
            {var subQ0=sQuery(id+"F6.wireOp",EDGE,"E13");Q11=makeQuery(id+"F7.boolean.opBoolean","COPY",EDGE,{"disambiguationData":[topologyDisambiguationEdgeConnected([makeQuery(id+"F7.opExtrude","SWEPT_FACE",FACE,{"disambiguationData":[OSD([subQ0])]}),makeQuery(id+"F7.opExtrude","CAP_FACE",FACE,{"disambiguationData":[OSD([sQuery(id+"F2.wireOp",EDGE,"E3"),sQuery(id+"F2.wireOp",EDGE,"E4"),sQuery(id+"F2.wireOp",EDGE,"E6"),subQ0])],"isStart":false})])],"derivedFrom":makeQuery(id+"F7.opExtrude","CAP_EDGE",EDGE,{"disambiguationData":[OSD([subQ0])],"isStart":false})});}
            fillet(context, id + "F12", {"entities" : qUnion([Q0, Q1, Q2, Q3, Q4, Q5, Q6, Q7, Q8, Q9, Q10, Q11]), "radius" : 0.5 * mm, "tangentPropagation" : true, "allowEdgeOverflow" : false});
        }
        {
            var Q0;
            Q0=makeQuery(id+"F9.boolean.opBoolean","COPY",FACE,{"derivedFrom":makeQuery(id+"F9.opExtrude","CAP_FACE",FACE,{"disambiguationData":[OSD([sQuery(id+"F0.wireOp",EDGE,"E0"),sQuery(id+"F0.wireOp",EDGE,"E1")])],"isStart":false})});
            extrude(context, id + "F13", {"entities" : qUnion([Q0]), "operationType" : NewBodyOperationType.ADD, "depth" : 22 * mm});
        }
        {
            var Q0;
            Q0=makeQuery(id+"F3.opRevolve","SWEPT_FACE",FACE,{"disambiguationData":[OSD([sQuery(id+"F2.wireOp",EDGE,"E3")])]});
            extrude(context, id + "F14", {"entities" : qUnion([Q0]), "operationType" : NewBodyOperationType.REMOVE, "oppositeDirection" : true, "depth" : 12 * mm});
        }
        {
            var Q0;
            Q0=makeQuery(id+"F13.opExtrude","SWEPT_FACE",FACE,{"disambiguationData":[OSD([sQuery(id+"F0.wireOp",EDGE,"E0")])]});
            chamfer(context, id + "F15", {"entities" : qUnion([Q0]), "width" : 0.7 * mm, "tangentPropagation" : true});
        }
    });
